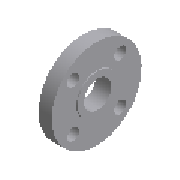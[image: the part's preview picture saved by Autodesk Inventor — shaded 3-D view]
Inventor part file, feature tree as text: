
AUTODESK INVENTOR PART (.ipt)
format: ipt  version: 2024.2 (Build 282272000, 272)  size: 202,240 bytes
history: native  units: mm (DEFAULTED — no unit token found)
features: other x7, revolve x1
ambient origin geometry x8: Origin, YZ Plane, XZ Plane, XY Plane, X Axis, Y Axis, Z Axis, Center Point
bodies: Solid1 (feature_tree)
feature tree (8):
  revolve  "Revolution1"  Angle=90.0deg
  other  "Work Axis3"
  other  "Work Point4"
  other  "Work Axis4"
  other  "Work Axis5"
  other  "Work Point5"
  other  "Work Axis6"
  other  "Work Point6"
